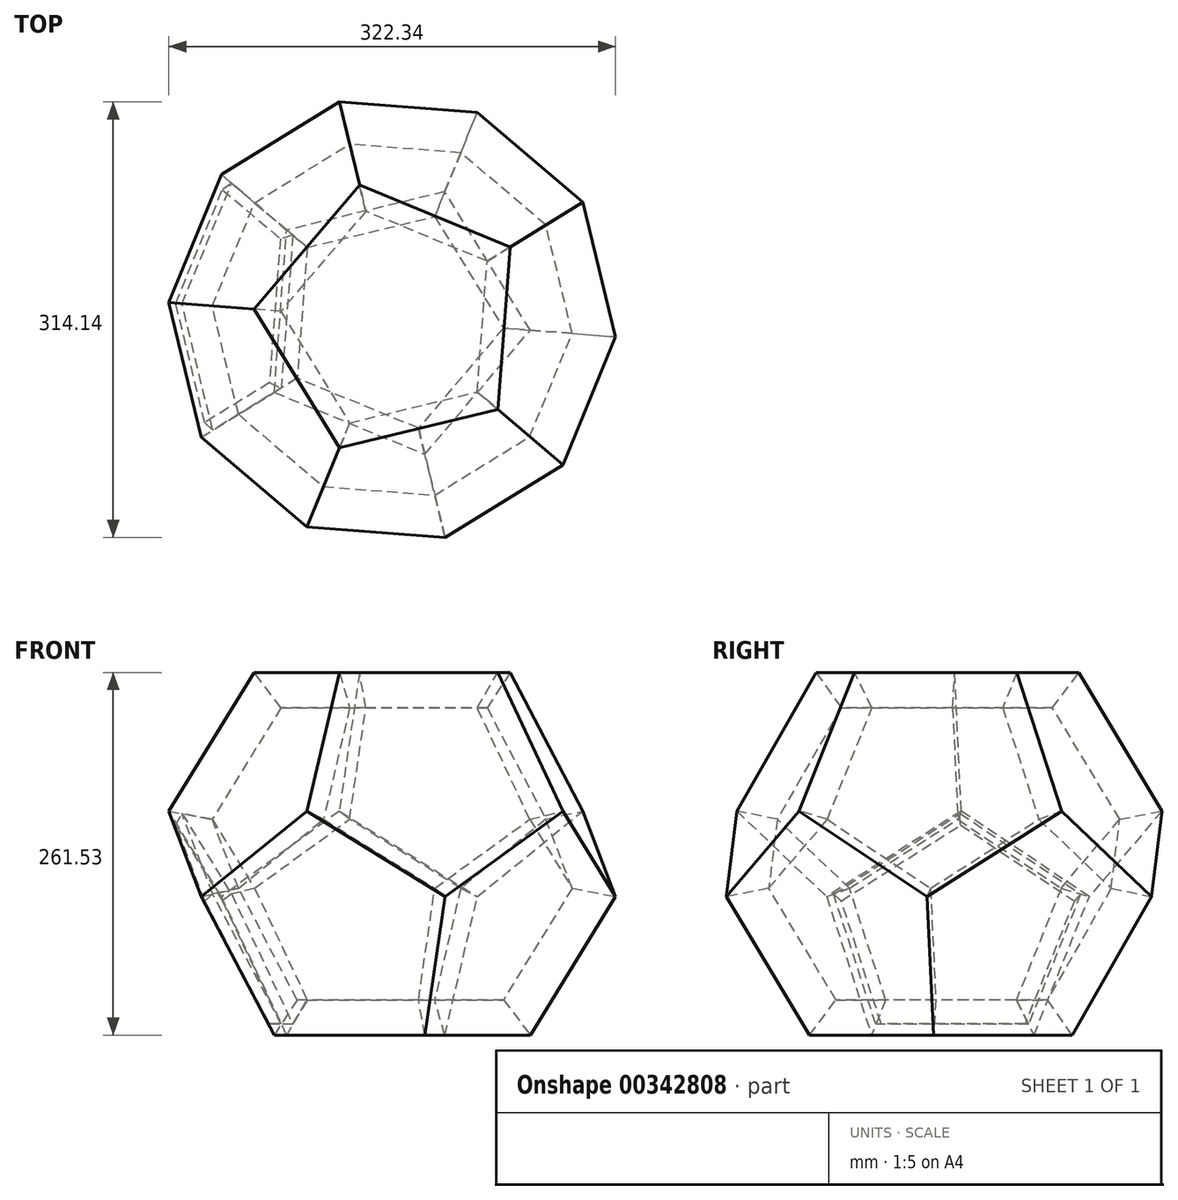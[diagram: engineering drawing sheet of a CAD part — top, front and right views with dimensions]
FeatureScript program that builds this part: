
annotation { "Feature Type Name" : "Feature", "Feature Type Description" : "" }
export const myFeature = defineFeature(function(context is Context, id is Id, definition is map)
    precondition{}
    {
        {
            var Q0;
            Q0=qCreatedBy(makeId("Top.planeOp"),FACE);
            var sketch = newSketch(context, id + "F0", { "sketchPlane" : qUnion([Q0])});
            skCircle(sketch, "E0.cCircle", {"center": v(0, 0) * mm, "radius": 80.82 * mm, "construction": true});
            skLineSegment(sketch, "E0.0", {"start": v(99.6, -7.58) * mm, "end": v(23.57, -97.07) * mm});
            skLineSegment(sketch, "E0.1", {"start": v(23.57, -97.07) * mm, "end": v(-85.04, -52.42) * mm});
            skLineSegment(sketch, "E0.2", {"start": v(-85.04, -52.42) * mm, "end": v(-76.13, 64.68) * mm});
            skLineSegment(sketch, "E0.3", {"start": v(-76.13, 64.68) * mm, "end": v(37.99, 92.39) * mm});
            skLineSegment(sketch, "E0.4", {"start": v(37.99, 92.39) * mm, "end": v(99.6, -7.58) * mm});
            skPoint(sketch, "E0.0.midPoint", {"position": v(61.59, -52.33) * mm});
            skSolve(sketch);
        }
        {
            var Q0;
            Q0=makeQuery(id+"F0.imprint","IMPRINT",FACE,{"disambiguationData":[TD([[makeQuery(id+"F0.imprint","IMPRINT",EDGE,{"derivedFrom":sQuery(id+"F0.wireOp",EDGE,"E0.0")}),-1.0]])]});
            extrude(context, id + "F1", {"entities" : qUnion([Q0]), "depth" : 25.4 * mm});
        }
        {
            var Q0;
            Q0=makeQuery(id+"F1.opExtrude","CAP_EDGE",EDGE,{"disambiguationData":[OSD([sQuery(id+"F0.wireOp",EDGE,"E0.1")])],"isStart":false});
            var Q1;
            Q1=makeQuery(id+"F1.opExtrude","CAP_EDGE",EDGE,{"disambiguationData":[OSD([sQuery(id+"F0.wireOp",EDGE,"E0.2")])],"isStart":false});
            var Q2;
            Q2=makeQuery(id+"F1.opExtrude","CAP_EDGE",EDGE,{"disambiguationData":[OSD([sQuery(id+"F0.wireOp",EDGE,"E0.3")])],"isStart":false});
            var Q3;
            Q3=makeQuery(id+"F1.opExtrude","CAP_EDGE",EDGE,{"disambiguationData":[OSD([sQuery(id+"F0.wireOp",EDGE,"E0.4")])],"isStart":false});
            var Q4;
            Q4=makeQuery(id+"F1.opExtrude","CAP_EDGE",EDGE,{"disambiguationData":[OSD([sQuery(id+"F0.wireOp",EDGE,"E0.0")])],"isStart":false});
            chamfer(context, id + "F2", {"entities" : qUnion([Q0, Q1, Q2, Q3, Q4]), "chamferType" : ChamferType.OFFSET_ANGLE, "width" : 25.4 * mm, "oppositeDirection" : false, "angle" : 31.72 * degree, "tangentPropagation" : true});
        }
        {
            var Q0;
            Q0=makeQuery(id+"F1.opExtrude","SWEPT_BODY",BODY,{"disambiguationData":[OSD([sQuery(id+"F0.wireOp",EDGE,"E0.0"),sQuery(id+"F0.wireOp",EDGE,"E0.1"),sQuery(id+"F0.wireOp",EDGE,"E0.2"),sQuery(id+"F0.wireOp",EDGE,"E0.3"),sQuery(id+"F0.wireOp",EDGE,"E0.4")])]});
            var Q1;
            Q1=makeQuery(id+"F2.opChamfer","BLEND_EDGE",EDGE,{"blendedFrom":[makeQuery(id+"F1.opExtrude","CAP_EDGE",EDGE,{"disambiguationData":[OSD([sQuery(id+"F0.wireOp",EDGE,"E0.1")])],"isStart":false}),makeQuery(id+"F1.opExtrude","CAP_EDGE",EDGE,{"disambiguationData":[OSD([sQuery(id+"F0.wireOp",EDGE,"E0.2")])],"isStart":false})],"blendedInto":[]});
            circularPattern(context, id + "F3", {"entities" : qUnion([Q0]), "axis" : qUnion([Q1]), "angle" : 360 * degree, "instanceCount" : 3, "equalSpace" : true});
        }
        {
            var Q0;
            Q0=makeQuery(id+"F1.opExtrude","SWEPT_BODY",BODY,{"disambiguationData":[OSD([sQuery(id+"F0.wireOp",EDGE,"E0.0"),sQuery(id+"F0.wireOp",EDGE,"E0.1"),sQuery(id+"F0.wireOp",EDGE,"E0.2"),sQuery(id+"F0.wireOp",EDGE,"E0.3"),sQuery(id+"F0.wireOp",EDGE,"E0.4")])]});
            var Q1;
            Q1=makeQuery(id+"F3.opPattern","COPY",BODY,{"derivedFrom":makeQuery(id+"F1.opExtrude","SWEPT_BODY",BODY,{"disambiguationData":[OSD([sQuery(id+"F0.wireOp",EDGE,"E0.0"),sQuery(id+"F0.wireOp",EDGE,"E0.1"),sQuery(id+"F0.wireOp",EDGE,"E0.2"),sQuery(id+"F0.wireOp",EDGE,"E0.3"),sQuery(id+"F0.wireOp",EDGE,"E0.4")])]}),"instanceName":"1"});
            var Q2;
            Q2=makeQuery(id+"F3.opPattern","COPY",BODY,{"derivedFrom":makeQuery(id+"F1.opExtrude","SWEPT_BODY",BODY,{"disambiguationData":[OSD([sQuery(id+"F0.wireOp",EDGE,"E0.0"),sQuery(id+"F0.wireOp",EDGE,"E0.1"),sQuery(id+"F0.wireOp",EDGE,"E0.2"),sQuery(id+"F0.wireOp",EDGE,"E0.3"),sQuery(id+"F0.wireOp",EDGE,"E0.4")])]}),"instanceName":"2"});
            var Q3;
            Q3=makeQuery(id+"F2.opChamfer","BLEND_EDGE",EDGE,{"blendedFrom":[makeQuery(id+"F1.opExtrude","CAP_EDGE",EDGE,{"disambiguationData":[OSD([sQuery(id+"F0.wireOp",EDGE,"E0.0")])],"isStart":false}),makeQuery(id+"F1.opExtrude","CAP_EDGE",EDGE,{"disambiguationData":[OSD([sQuery(id+"F0.wireOp",EDGE,"E0.4")])],"isStart":false})],"blendedInto":[]});
            transform(context, id + "F4", {"entities" : qUnion([Q0, Q1, Q2]), "transformType" : TransformType.ROTATION, "transformAxis" : qUnion([Q3]), "angle" : 120 * degree, "makeCopy" : true});
        }
        {
            var Q0;
            Q0=makeQuery(id+"F4.opPattern","COPY",BODY,{"derivedFrom":makeQuery(id+"F3.opPattern","COPY",BODY,{"derivedFrom":makeQuery(id+"F1.opExtrude","SWEPT_BODY",BODY,{"disambiguationData":[OSD([sQuery(id+"F0.wireOp",EDGE,"E0.0"),sQuery(id+"F0.wireOp",EDGE,"E0.1"),sQuery(id+"F0.wireOp",EDGE,"E0.2"),sQuery(id+"F0.wireOp",EDGE,"E0.3"),sQuery(id+"F0.wireOp",EDGE,"E0.4")])]}),"instanceName":"1"}),"instanceName":"1"});
            var Q1;
            Q1=makeQuery(id+"F4.opPattern","COPY",BODY,{"derivedFrom":makeQuery(id+"F3.opPattern","COPY",BODY,{"derivedFrom":makeQuery(id+"F1.opExtrude","SWEPT_BODY",BODY,{"disambiguationData":[OSD([sQuery(id+"F0.wireOp",EDGE,"E0.0"),sQuery(id+"F0.wireOp",EDGE,"E0.1"),sQuery(id+"F0.wireOp",EDGE,"E0.2"),sQuery(id+"F0.wireOp",EDGE,"E0.3"),sQuery(id+"F0.wireOp",EDGE,"E0.4")])]}),"instanceName":"2"}),"instanceName":"1"});
            var Q2;
            Q2=makeQuery(id+"F4.opPattern","COPY",BODY,{"derivedFrom":makeQuery(id+"F1.opExtrude","SWEPT_BODY",BODY,{"disambiguationData":[OSD([sQuery(id+"F0.wireOp",EDGE,"E0.0"),sQuery(id+"F0.wireOp",EDGE,"E0.1"),sQuery(id+"F0.wireOp",EDGE,"E0.2"),sQuery(id+"F0.wireOp",EDGE,"E0.3"),sQuery(id+"F0.wireOp",EDGE,"E0.4")])]}),"instanceName":"1"});
            var Q3;
            Q3=makeQuery(id+"F4.opPattern","COPY",EDGE,{"derivedFrom":makeQuery(id+"F3.opPattern","COPY",EDGE,{"derivedFrom":makeQuery(id+"F2.opChamfer","BLEND_EDGE",EDGE,{"blendedFrom":[makeQuery(id+"F1.opExtrude","CAP_EDGE",EDGE,{"disambiguationData":[OSD([sQuery(id+"F0.wireOp",EDGE,"E0.0")])],"isStart":false}),makeQuery(id+"F1.opExtrude","CAP_EDGE",EDGE,{"disambiguationData":[OSD([sQuery(id+"F0.wireOp",EDGE,"E0.4")])],"isStart":false})],"blendedInto":[]}),"instanceName":"2"}),"instanceName":"1"});
            transform(context, id + "F5", {"entities" : qUnion([Q0, Q1, Q2]), "transformType" : TransformType.ROTATION, "transformAxis" : qUnion([Q3]), "angle" : 120 * degree, "makeCopy" : true});
        }
        {
            var Q0;
            Q0=makeQuery(id+"F5.opPattern","COPY",BODY,{"derivedFrom":makeQuery(id+"F4.opPattern","COPY",BODY,{"derivedFrom":makeQuery(id+"F1.opExtrude","SWEPT_BODY",BODY,{"disambiguationData":[OSD([sQuery(id+"F0.wireOp",EDGE,"E0.0"),sQuery(id+"F0.wireOp",EDGE,"E0.1"),sQuery(id+"F0.wireOp",EDGE,"E0.2"),sQuery(id+"F0.wireOp",EDGE,"E0.3"),sQuery(id+"F0.wireOp",EDGE,"E0.4")])]}),"instanceName":"1"}),"instanceName":"1"});
            var Q1;
            Q1=makeQuery(id+"F4.opPattern","COPY",BODY,{"derivedFrom":makeQuery(id+"F3.opPattern","COPY",BODY,{"derivedFrom":makeQuery(id+"F1.opExtrude","SWEPT_BODY",BODY,{"disambiguationData":[OSD([sQuery(id+"F0.wireOp",EDGE,"E0.0"),sQuery(id+"F0.wireOp",EDGE,"E0.1"),sQuery(id+"F0.wireOp",EDGE,"E0.2"),sQuery(id+"F0.wireOp",EDGE,"E0.3"),sQuery(id+"F0.wireOp",EDGE,"E0.4")])]}),"instanceName":"2"}),"instanceName":"1"});
            var Q2;
            Q2=makeQuery(id+"F5.opPattern","COPY",BODY,{"derivedFrom":makeQuery(id+"F4.opPattern","COPY",BODY,{"derivedFrom":makeQuery(id+"F3.opPattern","COPY",BODY,{"derivedFrom":makeQuery(id+"F1.opExtrude","SWEPT_BODY",BODY,{"disambiguationData":[OSD([sQuery(id+"F0.wireOp",EDGE,"E0.0"),sQuery(id+"F0.wireOp",EDGE,"E0.1"),sQuery(id+"F0.wireOp",EDGE,"E0.2"),sQuery(id+"F0.wireOp",EDGE,"E0.3"),sQuery(id+"F0.wireOp",EDGE,"E0.4")])]}),"instanceName":"2"}),"instanceName":"1"}),"instanceName":"1"});
            var Q3;
            Q3=makeQuery(id+"F5.opPattern","COPY",EDGE,{"derivedFrom":makeQuery(id+"F4.opPattern","COPY",EDGE,{"derivedFrom":makeQuery(id+"F3.opPattern","COPY",EDGE,{"derivedFrom":makeQuery(id+"F2.opChamfer","BLEND_EDGE",EDGE,{"blendedFrom":[makeQuery(id+"F1.opExtrude","CAP_EDGE",EDGE,{"disambiguationData":[OSD([sQuery(id+"F0.wireOp",EDGE,"E0.2")])],"isStart":false}),makeQuery(id+"F1.opExtrude","CAP_EDGE",EDGE,{"disambiguationData":[OSD([sQuery(id+"F0.wireOp",EDGE,"E0.3")])],"isStart":false})],"blendedInto":[]}),"instanceName":"2"}),"instanceName":"1"}),"instanceName":"1"});
            transform(context, id + "F6", {"entities" : qUnion([Q0, Q1, Q2]), "transformType" : TransformType.ROTATION, "transformAxis" : qUnion([Q3]), "angle" : 240 * degree, "makeCopy" : true});
        }
        {
            var Q0;
            Q0=makeQuery(id+"F3.opPattern","COPY",FACE,{"derivedFrom":makeQuery(id+"F1.opExtrude","CAP_FACE",FACE,{"disambiguationData":[OSD([sQuery(id+"F0.wireOp",EDGE,"E0.0"),sQuery(id+"F0.wireOp",EDGE,"E0.1"),sQuery(id+"F0.wireOp",EDGE,"E0.2"),sQuery(id+"F0.wireOp",EDGE,"E0.3"),sQuery(id+"F0.wireOp",EDGE,"E0.4")])],"isStart":true}),"instanceName":"2"});
            chamfer(context, id + "F7", {"entities" : qUnion([Q0]), "width" : 5.08 * mm, "tangentPropagation" : true});
        }
    });
